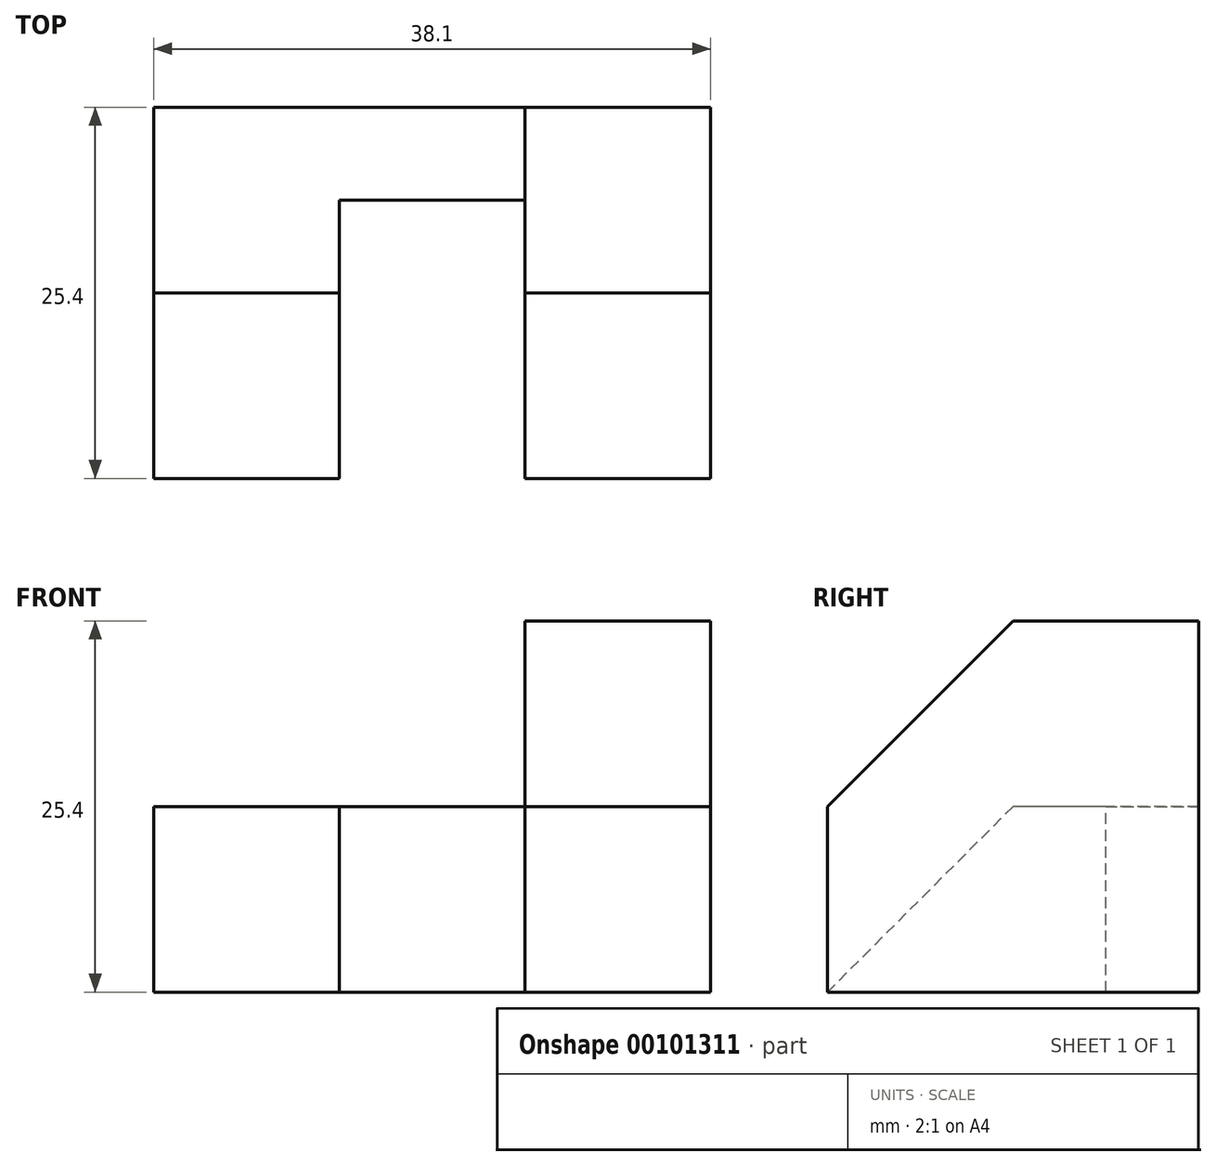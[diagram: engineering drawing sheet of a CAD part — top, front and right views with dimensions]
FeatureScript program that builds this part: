
annotation { "Feature Type Name" : "Feature", "Feature Type Description" : "" }
export const myFeature = defineFeature(function(context is Context, id is Id, definition is map)
    precondition{}
    {
        {
            var Q0;
            Q0=qCreatedBy(makeId("Right.planeOp"),FACE);
            var sketch = newSketch(context, id + "F0", { "sketchPlane" : qUnion([Q0])});
            skLineSegment(sketch, "E0", {"start": v(0, 0) * mm, "end": v(25.4, 0) * mm});
            skLineSegment(sketch, "E1", {"start": v(25.4, 0) * mm, "end": v(25.4, 25.4) * mm});
            skLineSegment(sketch, "E2", {"start": v(25.4, 25.4) * mm, "end": v(12.7, 25.4) * mm});
            skLineSegment(sketch, "E3", {"start": v(12.7, 25.4) * mm, "end": v(0, 12.7) * mm});
            skLineSegment(sketch, "E4", {"start": v(0, 12.7) * mm, "end": v(0, 0) * mm});
            skSolve(sketch);
        }
        {
            var Q0;
            Q0 = qSketchRegion(id + "F0", true);
            extrude(context, id + "F1", {"entities" : qUnion([Q0]), "oppositeDirection" : true, "depth" : 12.7 * mm});
        }
        {
            var Q0;
            Q0=makeQuery(id+"F1.opExtrude","SWEPT_FACE",FACE,{"disambiguationData":[OSD([sQuery(id+"F0.wireOp",EDGE,"E1")])]});
            var sketch = newSketch(context, id + "F2", { "sketchPlane" : qUnion([Q0])});
            skLineSegment(sketch, "E5", {"start": v(12.7, 0) * mm, "end": v(12.7, 12.7) * mm});
            skLineSegment(sketch, "E6", {"start": v(12.7, 12.7) * mm, "end": v(25.4, 12.7) * mm});
            skLineSegment(sketch, "E7", {"start": v(25.4, 12.7) * mm, "end": v(25.4, 0) * mm});
            skLineSegment(sketch, "E8", {"start": v(25.4, 0) * mm, "end": v(12.7, 0) * mm});
            skSolve(sketch);
        }
        {
            var Q0;
            Q0 = qSketchRegion(id + "F2", true);
            extrude(context, id + "F3", {"entities" : qUnion([Q0]), "oppositeDirection" : true, "depth" : 6.35 * mm});
        }
        {
            var Q0;
            Q0=makeQuery(id+"F3.opExtrude","SWEPT_FACE",FACE,{"disambiguationData":[OSD([sQuery(id+"F2.wireOp",EDGE,"E7")])]});
            var sketch = newSketch(context, id + "F4", { "sketchPlane" : qUnion([Q0])});
            skLineSegment(sketch, "E9", {"start": v(-25.4, 12.7) * mm, "end": v(-12.7, 12.7) * mm});
            skLineSegment(sketch, "E10", {"start": v(-12.7, 12.7) * mm, "end": v(0, 0) * mm});
            skLineSegment(sketch, "E11", {"start": v(0, 0) * mm, "end": v(-25.4, 0) * mm});
            skLineSegment(sketch, "E12", {"start": v(-25.4, 0) * mm, "end": v(-25.4, 12.7) * mm});
            skSolve(sketch);
        }
        {
            var Q0;
            Q0 = qSketchRegion(id + "F4", true);
            extrude(context, id + "F5", {"entities" : qUnion([Q0]), "operationType" : NewBodyOperationType.ADD, "depth" : 12.7 * mm});
        }
    });
